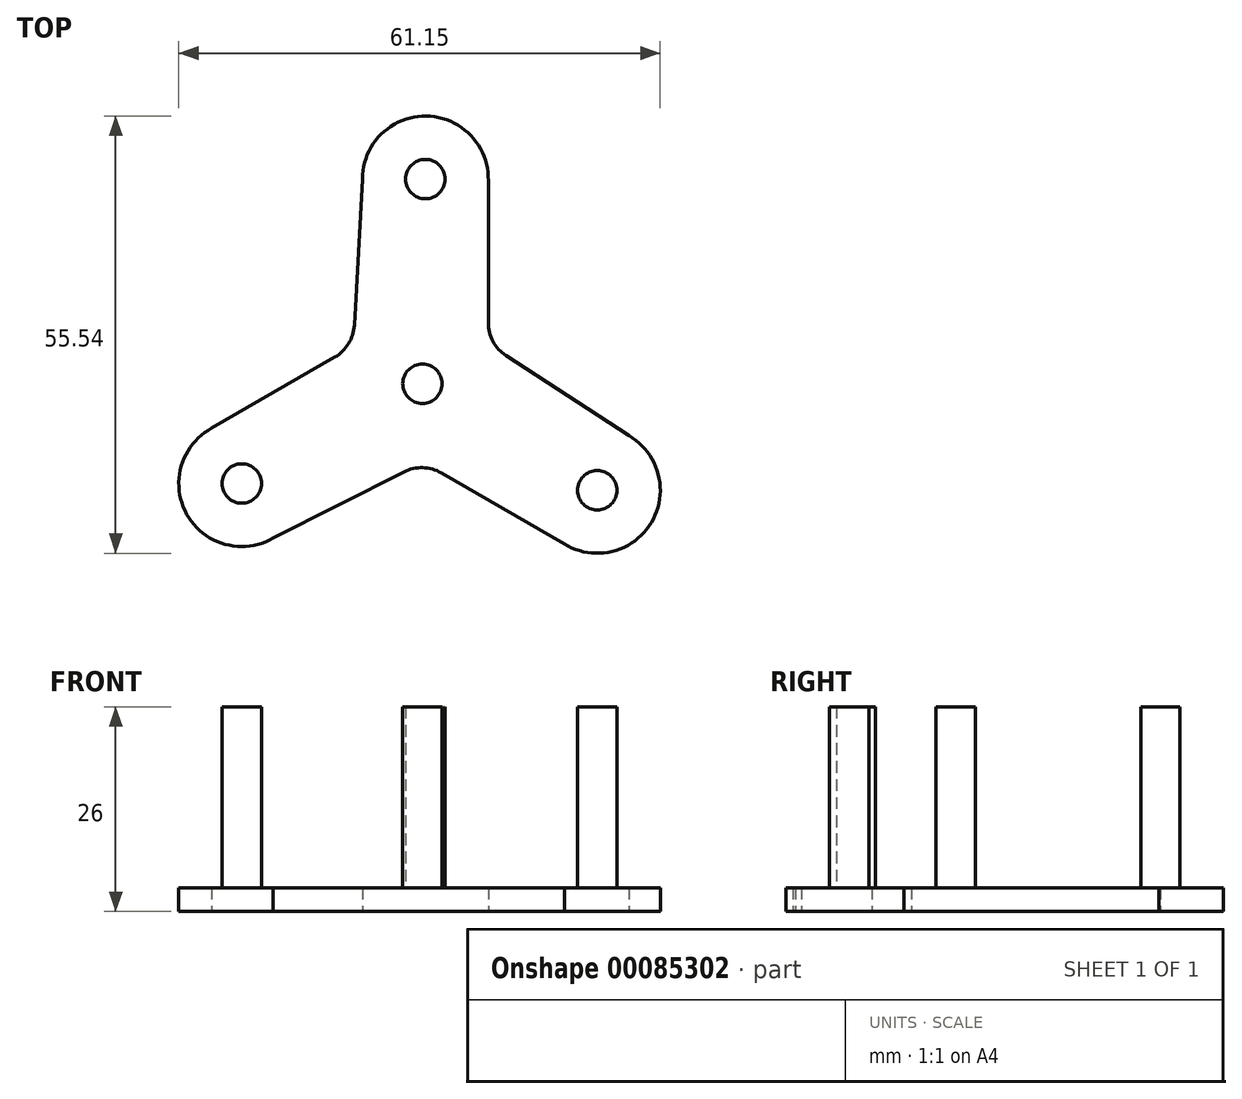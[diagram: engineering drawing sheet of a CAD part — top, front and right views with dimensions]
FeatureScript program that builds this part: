
annotation { "Feature Type Name" : "Feature", "Feature Type Description" : "" }
export const myFeature = defineFeature(function(context is Context, id is Id, definition is map)
    precondition{}
    {
        {
            var Q0;
            Q0=qCreatedBy(makeId("Top.planeOp"),FACE);
            var sketch = newSketch(context, id + "F0", { "sketchPlane" : qUnion([Q0])});
            skCircle(sketch, "E0", {"center": v(0, 0) * mm, "radius": 2.5 * mm});
            skCircle(sketch, "E1", {"center": v(0.37, 26) * mm, "radius": 2.5 * mm});
            skLineSegment(sketch, "E2", {"start": v(0.37, 26) * mm, "end": v(0, 0) * mm});
            skArc(sketch, "E3", {"start": v(8.37, 25.78) * mm, "mid": v(0.48, 34) * mm, "end": v(-7.63, 26) * mm});
            skCircle(sketch, "E4", {"center": v(0, 0) * mm, "radius": 9 * mm});
            skLineSegment(sketch, "E5", {"start": v(-8.65, 7.43) * mm, "end": v(-7.63, 26) * mm});
            skLineSegment(sketch, "E6", {"start": v(8.37, 25.78) * mm, "end": v(8.37, 7.75) * mm});
            skLineSegment(sketch, "E7.1.0", {"start": v(-2.36, -11.2) * mm, "end": v(-18.95, -19.6) * mm});
            skArc(sketch, "E7.1.1", {"start": v(-26.76, -5.65) * mm, "mid": v(-29.93, -16.59) * mm, "end": v(-18.95, -19.6) * mm});
            skLineSegment(sketch, "E7.1.2", {"start": v(-26.76, -5.65) * mm, "end": v(-11.15, 3.37) * mm});
            skCircle(sketch, "E7.1.3", {"center": v(-22.95, -12.68) * mm, "radius": 2.5 * mm});
            skLineSegment(sketch, "E7.1.4", {"start": v(-22.95, -12.68) * mm, "end": v(-0.25, 0) * mm});
            skLineSegment(sketch, "E7.2.0", {"start": v(10.63, 3.56) * mm, "end": v(26.2, -6.6) * mm});
            skArc(sketch, "E7.2.1", {"start": v(18.02, -20.35) * mm, "mid": v(29.08, -17.63) * mm, "end": v(26.2, -6.6) * mm});
            skLineSegment(sketch, "E7.2.2", {"start": v(18.02, -20.35) * mm, "end": v(2.4, -11.34) * mm});
            skCircle(sketch, "E7.2.3", {"center": v(22.2, -13.54) * mm, "radius": 2.5 * mm});
            skLineSegment(sketch, "E7.2.4", {"start": v(22.2, -13.54) * mm, "end": v(-0.13, -0.22) * mm});
            skPoint(sketch, "E7.center", {"position": v(-0.13, -0.07) * mm});
            skPoint(sketch, "E8.newPointA", {"position": v(-4.44, 7.24) * mm});
            skPoint(sketch, "E8.newPointB", {"position": v(-9.06, 0) * mm});
            skArc(sketch, "E8.filletArc", {"start": v(-11.15, 3.37) * mm, "mid": v(-9.39, 5.08) * mm, "end": v(-8.65, 7.43) * mm});
            skArc(sketch, "E9.1.0", {"start": v(2.4, -11.34) * mm, "mid": v(0.04, -10.67) * mm, "end": v(-2.36, -11.2) * mm});
            skArc(sketch, "E9.2.0", {"start": v(8.37, 7.75) * mm, "mid": v(8.97, 5.37) * mm, "end": v(10.63, 3.56) * mm});
            skPoint(sketch, "E10.orphan", {"position": v(8.37, 0) * mm});
            skPoint(sketch, "E11.orphan", {"position": v(4.4, 7.63) * mm});
            skPoint(sketch, "E12.orphan", {"position": v(4.28, -7.85) * mm});
            skSolve(sketch);
        }
        {
            var Q0;
            Q0=qSketchRegion(id+"F0",true);
            var Q1;
            {var subQ0=sQuery(id+"F0.wireOp",EDGE,"E7.1.4");var subQ1=sQuery(id+"F0.wireOp",EDGE,"E0");var subQ2=makeQuery(id+"F0.imprint","INTERSECT",VERTEX,{"derivedFrom":[subQ1,subQ0]});Q1=makeQuery(id+"F0.imprint","IMPRINT",FACE,{"disambiguationData":[TD([[makeQuery(id+"F0.imprint","IMPRINT",EDGE,{"disambiguationData":[TD([[subQ2,-1.0]])],"derivedFrom":subQ1}),-1.0]])]});}
            var Q2;
            {var subQ0=sQuery(id+"F0.wireOp",EDGE,"E7.1.4");var subQ1=sQuery(id+"F0.wireOp",EDGE,"E0");var subQ2=makeQuery(id+"F0.imprint","INTERSECT",VERTEX,{"derivedFrom":[subQ1,subQ0]});Q2=makeQuery(id+"F0.imprint","IMPRINT",FACE,{"disambiguationData":[TD([[makeQuery(id+"F0.imprint","IMPRINT",EDGE,{"disambiguationData":[TD([[subQ2,1.0]])],"derivedFrom":subQ1}),-1.0]])]});}
            var Q3;
            {var subQ0=sQuery(id+"F0.wireOp",EDGE,"E2");var subQ1=sQuery(id+"F0.wireOp",EDGE,"E0");var subQ2=makeQuery(id+"F0.imprint","INTERSECT",VERTEX,{"derivedFrom":[subQ1,subQ0]});Q3=makeQuery(id+"F0.imprint","IMPRINT",FACE,{"disambiguationData":[TD([[makeQuery(id+"F0.imprint","IMPRINT",EDGE,{"disambiguationData":[TD([[subQ2,1.0]])],"derivedFrom":subQ1}),-1.0]])]});}
            var Q4;
            Q4=makeQuery(id+"F0.imprint","IMPRINT",FACE,{"disambiguationData":[TD([[makeQuery(id+"F0.imprint","IMPRINT",EDGE,{"derivedFrom":sQuery(id+"F0.wireOp",EDGE,"E1")}),1.0]])]});
            var Q5;
            Q5=makeQuery(id+"F0.imprint","IMPRINT",FACE,{"disambiguationData":[TD([[makeQuery(id+"F0.imprint","IMPRINT",EDGE,{"derivedFrom":sQuery(id+"F0.wireOp",EDGE,"E7.2.3")}),1.0]])]});
            var Q6;
            {var subQ0=sQuery(id+"F0.wireOp",EDGE,"E0");var subQ1=makeQuery(id+"F0.imprint","INTERSECT",VERTEX,{"derivedFrom":[subQ0,sQuery(id+"F0.wireOp",EDGE,"E7.1.4")]});Q6=makeQuery(id+"F0.imprint","IMPRINT",FACE,{"disambiguationData":[TD([[makeQuery(id+"F0.imprint","IMPRINT",EDGE,{"disambiguationData":[TD([[subQ1,1.0]])],"derivedFrom":subQ0}),1.0]])]});}
            var Q7;
            Q7=makeQuery(id+"F0.imprint","IMPRINT",FACE,{"disambiguationData":[TD([[makeQuery(id+"F0.imprint","IMPRINT",EDGE,{"derivedFrom":sQuery(id+"F0.wireOp",EDGE,"E7.1.3")}),1.0]])]});
            extrude(context, id + "F1", {"entities" : qUnion([Q0, Q1, Q2, Q3, Q4, Q5, Q6, Q7]), "depth" : 3 * mm});
        }
        {
            var Q0;
            Q0=makeQuery(id+"F1.opExtrude","CAP_FACE",FACE,{"disambiguationData":[OSD([sQuery(id+"F0.wireOp",EDGE,"E3"),sQuery(id+"F0.wireOp",EDGE,"E5"),sQuery(id+"F0.wireOp",EDGE,"E6"),sQuery(id+"F0.wireOp",EDGE,"E7.1.0"),sQuery(id+"F0.wireOp",EDGE,"E7.1.1"),sQuery(id+"F0.wireOp",EDGE,"E7.1.2"),sQuery(id+"F0.wireOp",EDGE,"E7.2.0"),sQuery(id+"F0.wireOp",EDGE,"E7.2.1"),sQuery(id+"F0.wireOp",EDGE,"E7.2.2"),sQuery(id+"F0.wireOp",EDGE,"E8.filletArc"),sQuery(id+"F0.wireOp",EDGE,"E9.1.0"),sQuery(id+"F0.wireOp",EDGE,"E9.2.0")])],"isStart":false});
            var sketch = newSketch(context, id + "F2", { "sketchPlane" : qUnion([Q0])});
            skCircle(sketch, "E13", {"center": v(-22.95, -12.68) * mm, "radius": 8 * mm});
            skPoint(sketch, "E13.first.point", {"position": v(-29.58, -8.2) * mm});
            skPoint(sketch, "E13.second.point", {"position": v(-29.93, -16.59) * mm});
            skPoint(sketch, "E13.third.point", {"position": v(-22.27, -20.65) * mm});
            skCircle(sketch, "E14", {"center": v(0.37, 26) * mm, "radius": 8 * mm});
            skPoint(sketch, "E14.first.point", {"position": v(-6.8, 29.55) * mm});
            skPoint(sketch, "E14.second.point", {"position": v(0, 33.99) * mm});
            skPoint(sketch, "E14.third.point", {"position": v(7.37, 29.86) * mm});
            skCircle(sketch, "E15", {"center": v(22.2, -13.54) * mm, "radius": 8 * mm});
            skPoint(sketch, "E15.first.point", {"position": v(23.54, -21.42) * mm});
            skPoint(sketch, "E15.second.point", {"position": v(29.08, -17.63) * mm});
            skPoint(sketch, "E15.third.point", {"position": v(29.08, -9.44) * mm});
            skPoint(sketch, "E15.third.point.positionSnap0", {"position": v(29.08, -17.63) * mm});
            skCircle(sketch, "E16", {"center": v(0.37, 26) * mm, "radius": 2.5 * mm});
            skCircle(sketch, "E17", {"center": v(-22.95, -12.68) * mm, "radius": 2.5 * mm});
            skCircle(sketch, "E18", {"center": v(22.2, -13.54) * mm, "radius": 2.5 * mm});
            skCircle(sketch, "E19", {"center": v(0, 0) * mm, "radius": 2.5 * mm});
            skSolve(sketch);
        }
        {
            var Q0;
            Q0=makeQuery(id+"F2.imprint","IMPRINT",FACE,{"disambiguationData":[TD([[makeQuery(id+"F2.imprint","IMPRINT",EDGE,{"derivedFrom":sQuery(id+"F2.wireOp",EDGE,"E17")}),1.0]])]});
            var Q1;
            Q1=makeQuery(id+"F2.imprint","IMPRINT",FACE,{"disambiguationData":[TD([[makeQuery(id+"F2.imprint","IMPRINT",EDGE,{"derivedFrom":sQuery(id+"F2.wireOp",EDGE,"E16")}),1.0]])]});
            var Q2;
            Q2=makeQuery(id+"F2.imprint","IMPRINT",FACE,{"disambiguationData":[TD([[makeQuery(id+"F2.imprint","IMPRINT",EDGE,{"derivedFrom":sQuery(id+"F2.wireOp",EDGE,"E18")}),1.0]])]});
            var Q3;
            Q3=makeQuery(id+"F2.imprint","IMPRINT",FACE,{"disambiguationData":[TD([[makeQuery(id+"F2.imprint","IMPRINT",EDGE,{"derivedFrom":sQuery(id+"F2.wireOp",EDGE,"E19")}),1.0]])]});
            extrude(context, id + "F3", {"entities" : qUnion([Q0, Q1, Q2, Q3]), "operationType" : NewBodyOperationType.ADD, "depth" : 23 * mm});
        }
    });
